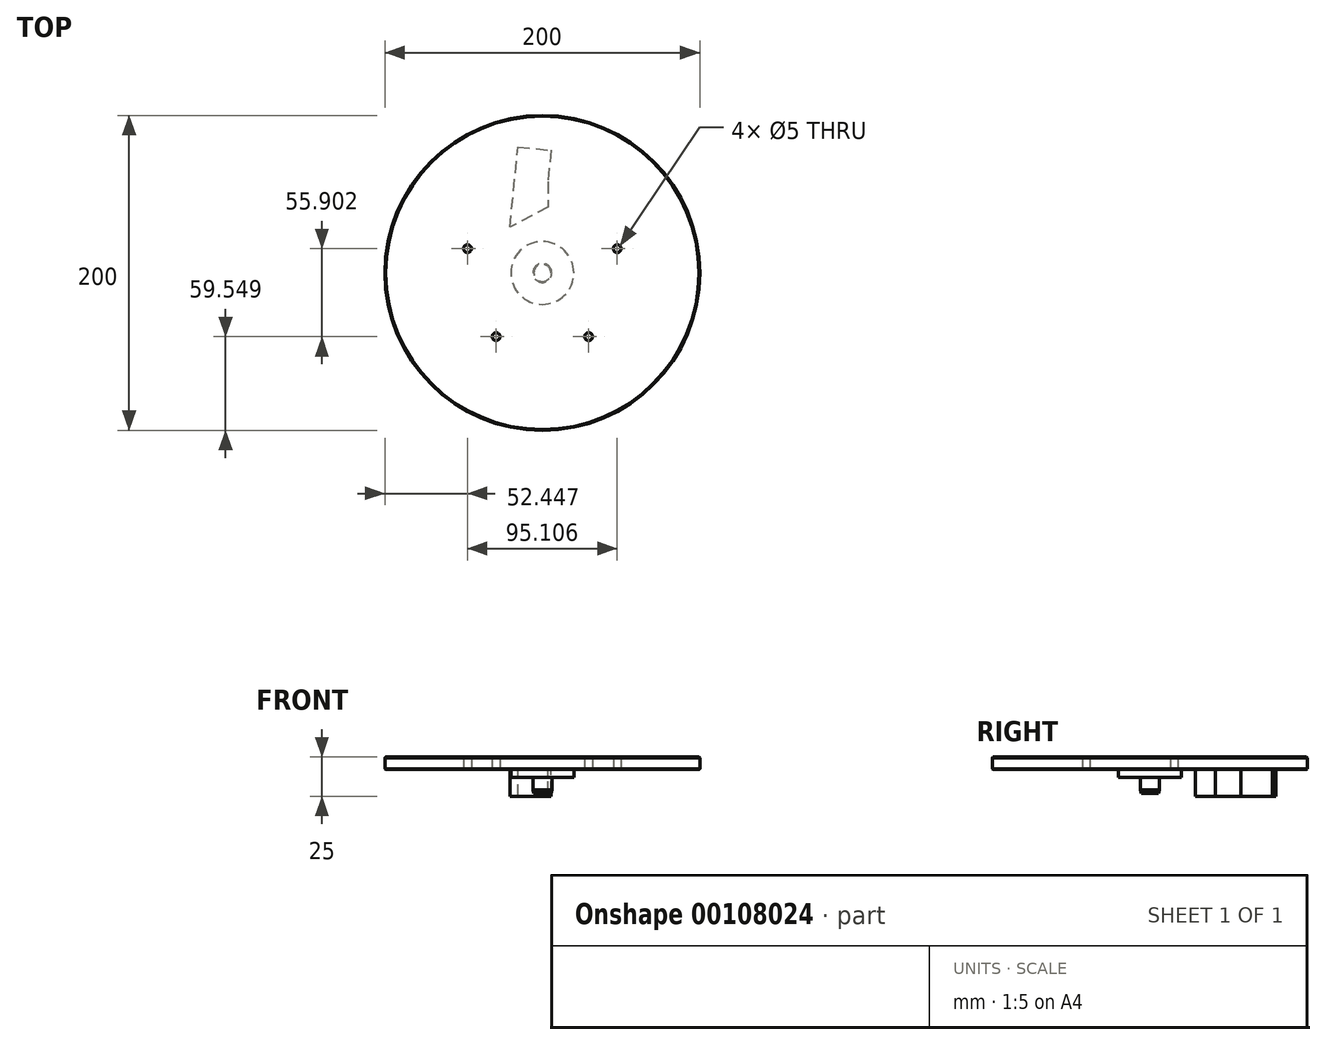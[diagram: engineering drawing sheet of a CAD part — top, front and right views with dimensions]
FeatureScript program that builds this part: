
annotation { "Feature Type Name" : "Feature", "Feature Type Description" : "" }
export const myFeature = defineFeature(function(context is Context, id is Id, definition is map)
    precondition{}
    {
        {
            var Q0;
            Q0=qCreatedBy(makeId("Front.planeOp"),FACE);
            var sketch = newSketch(context, id + "F0", { "sketchPlane" : qUnion([Q0])});
            skLineSegment(sketch, "E0", {"start": v(0, 0) * mm, "end": v(-100, 0) * mm});
            skLineSegment(sketch, "E1", {"start": v(-100, 0) * mm, "end": v(-100, -8) * mm});
            skLineSegment(sketch, "E2", {"start": v(-100, -8) * mm, "end": v(0, -8) * mm});
            skLineSegment(sketch, "E3", {"start": v(0, -8) * mm, "end": v(0, 0) * mm});
            skLineSegment(sketch, "E4", {"start": v(-20, -8) * mm, "end": v(-20, -13) * mm});
            skLineSegment(sketch, "E5", {"start": v(-20, -13) * mm, "end": v(-6, -13) * mm});
            skLineSegment(sketch, "E6", {"start": v(-6, -13) * mm, "end": v(-6, -21) * mm});
            skLineSegment(sketch, "E7", {"start": v(-5.46, -23) * mm, "end": v(-6, -21) * mm});
            skLineSegment(sketch, "E8", {"start": v(0, -93.82) * mm, "end": v(0, -93.82) * mm});
            skLineSegment(sketch, "E9", {"start": v(0, -23) * mm, "end": v(0, -8) * mm});
            skLineSegment(sketch, "E10", {"start": v(-5.46, -23) * mm, "end": v(0, -23) * mm});
            skLineSegment(sketch, "E11", {"start": v(-9.09, -13) * mm, "end": v(-15.53, -9.08) * mm});
            skSolve(sketch);
        }
        {
            var Q0;
            Q0=makeQuery(id+"F0.imprint","IMPRINT",FACE,{"disambiguationData":[TD([[makeQuery(id+"F0.imprint","IMPRINT",EDGE,{"derivedFrom":sQuery(id+"F0.wireOp",EDGE,"E0")}),1.0]])]});
            var Q1;
            Q1=sQuery(id+"F0.wireOp",EDGE,"E3");
            revolve(context, id + "F1", {"surfaceOperationType" : NewSurfaceOperationType.NEW, "entities" : qUnion([Q0]), "axis" : qUnion([Q1]), "revolveType" : RevolveType.FULL});
        }
        {
            var Q0;
            {var subQ0=sQuery(id+"F0.wireOp",EDGE,"E6");var subQ1=sQuery(id+"F0.wireOp",EDGE,"E5");var subQ2=makeQuery(id+"F0.imprint","INTERSECT",VERTEX,{"derivedFrom":[subQ1,subQ0]});Q0=makeQuery(id+"F0.imprint","IMPRINT",FACE,{"disambiguationData":[TD([[makeQuery(id+"F0.imprint","IMPRINT",EDGE,{"disambiguationData":[TD([[subQ2,1.0]])],"derivedFrom":subQ1}),-1.0]])]});}
            var Q1;
            {var subQ5=sQuery(id+"F0.wireOp",EDGE,"E4");Q1=makeQuery(id+"F0.imprint","IMPRINT",FACE,{"disambiguationData":[TD([[makeQuery(id+"F0.imprint","IMPRINT",EDGE,{"derivedFrom":subQ5}),1.0]])]});}
            var Q2;
            Q2=sQuery(id+"F0.wireOp",EDGE,"E3");
            revolve(context, id + "F2", {"surfaceOperationType" : NewSurfaceOperationType.NEW, "entities" : qUnion([Q0, Q1]), "axis" : qUnion([Q2]), "revolveType" : RevolveType.FULL});
        }
        {
            var Q0;
            Q0=makeQuery(id+"F1.opRevolve","SWEPT_FACE",FACE,{"disambiguationData":[OSD([sQuery(id+"F0.wireOp",EDGE,"E0")])]});
            var sketch = newSketch(context, id + "F3", { "sketchPlane" : qUnion([Q0])});
            skSolve(sketch);
        }
        {
            var Q0;
            Q0=makeQuery(id+"F1.opRevolve","SWEPT_EDGE",EDGE,{"disambiguationData":[OSD([sQuery(id+"F0.wireOp",EDGE,"E0"),sQuery(id+"F0.wireOp",EDGE,"E1")])]});
            var Q1;
            Q1=makeQuery(id+"F1.opRevolve","SWEPT_EDGE",EDGE,{"disambiguationData":[OSD([sQuery(id+"F0.wireOp",EDGE,"E1"),sQuery(id+"F0.wireOp",EDGE,"E2")])]});
            chamfer(context, id + "F4", {"entities" : qUnion([Q0, Q1]), "width" : 0.5 * mm, "tangentPropagation" : true});
        }
        {
            var Q0;
            Q0=makeQuery(id+"F3.imprint","IMPRINT",FACE,{"disambiguationData":[TD([[makeQuery(id+"F3.imprint","IMPRINT",EDGE,{"derivedFrom":makeQuery(id+"F1.opRevolve","SWEPT_EDGE",EDGE,{"disambiguationData":[OSD([sQuery(id+"F0.wireOp",EDGE,"E0"),sQuery(id+"F0.wireOp",EDGE,"E1")])]})}),-1.0]])]});
            var sketch = newSketch(context, id + "F5", { "sketchPlane" : qUnion([Q0])});
            skPoint(sketch, "E12", {"position": v(-47.55, 15.45) * mm});
            skPoint(sketch, "E13", {"position": v(0, 50) * mm});
            skPoint(sketch, "E14", {"position": v(47.55, 15.45) * mm});
            skPoint(sketch, "E15", {"position": v(29.39, -40.45) * mm});
            skPoint(sketch, "E16", {"position": v(-29.39, -40.45) * mm});
            skCircle(sketch, "E17", {"center": v(0, 0) * mm, "radius": 50 * mm});
            skLineSegment(sketch, "E18", {"start": v(0, 0) * mm, "end": v(0, 50) * mm});
            skLineSegment(sketch, "E19", {"start": v(0, 0) * mm, "end": v(-47.55, 15.45) * mm});
            skLineSegment(sketch, "E20", {"start": v(-29.39, -40.45) * mm, "end": v(0, 0) * mm});
            skLineSegment(sketch, "E21", {"start": v(29.39, -40.45) * mm, "end": v(0, 0) * mm});
            skLineSegment(sketch, "E22", {"start": v(47.55, 15.45) * mm, "end": v(0, 0) * mm});
            skSolve(sketch);
        }
        {
            var Q0;
            Q0=sQuery(id+"F5.wireOp",VERTEX,"E13");
            var Q1;
            Q1=sQuery(id+"F5.wireOp",VERTEX,"E12");
            var Q2;
            Q2=sQuery(id+"F5.wireOp",VERTEX,"E16");
            var Q3;
            Q3=sQuery(id+"F5.wireOp",VERTEX,"E15");
            var Q4;
            Q4=sQuery(id+"F5.wireOp",VERTEX,"E14");
            var Q5;
            Q5=makeQuery(id+"F1.opRevolve","SWEPT_BODY",BODY,{"disambiguationData":[OSD([sQuery(id+"F0.wireOp",EDGE,"E0"),sQuery(id+"F0.wireOp",EDGE,"E1"),sQuery(id+"F0.wireOp",EDGE,"E2"),sQuery(id+"F0.wireOp",EDGE,"E3")])]});
            hole(context, id + "F6", {"style" : HoleStyle.SIMPLE, "endStyle" : HoleEndStyle.THROUGH, "holeDiameter" : 5 * mm, "majorDiameter" : 5 * mm, "isTappedThrough" : true, "tappedDepth" : 12 * mm, "tapClearance" : 3, "locations" : qUnion([Q0, Q1, Q2, Q3, Q4]), "scope" : qUnion([Q5])});
        }
        {
            var Q0;
            Q0=qCreatedBy(makeId("Top.planeOp"),FACE);
            var sketch = newSketch(context, id + "F7", { "sketchPlane" : qUnion([Q0])});
            skLineSegment(sketch, "E23", {"start": v(-20.56, 29.1) * mm, "end": v(-15.47, 80.06) * mm});
            skLineSegment(sketch, "E24", {"start": v(-15.47, 80.06) * mm, "end": v(5.47, 77.97) * mm});
            skLineSegment(sketch, "E25", {"start": v(5.47, 77.97) * mm, "end": v(3.46, 57.9) * mm});
            skLineSegment(sketch, "E26", {"start": v(3.46, 57.9) * mm, "end": v(3.46, 41.82) * mm});
            skLineSegment(sketch, "E27", {"start": v(3.46, 41.82) * mm, "end": v(-20.56, 29.1) * mm});
            skSolve(sketch);
        }
        {
            var Q0;
            Q0 = qSketchRegion(id + "F7", true);
            extrude(context, id + "F8", {"entities" : qUnion([Q0]), "operationType" : NewBodyOperationType.ADD, "oppositeDirection" : true, "depth" : 25 * mm, "offsetDistance" : 25 * mm});
        }
    });
